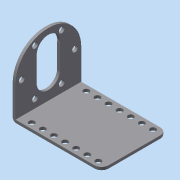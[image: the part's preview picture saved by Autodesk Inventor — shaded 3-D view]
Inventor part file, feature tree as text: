
AUTODESK INVENTOR PART (.ipt)
format: ipt  version: 2014 SP2 (Build 180246200, 246)  size: 179,712 bytes
history: native  units: mm
features: sketch x4, extrude x3, fillet x3, hole x1, pattern_linear x1
ambient origin geometry x8: Origin, YZ Plane, XZ Plane, XY Plane, X Axis, Y Axis, Z Axis, Center Point
bodies: Volumenkörper1 (feature_tree)
feature tree (12):
  extrude  "Extrusion1"  Depth=50.8mm
  extrude  "Extrusion2"  Depth=37.59mm
  extrude  "Extrusion3"  Depth=13.21mm
  fillet  "Rundung1"  Radius=11.0mm
  fillet  "Rundung2"  Radius=19.0mm
  fillet  "Rundung3"  Radius=30.5mm
  hole  "Bohrung2"  [1 undecoded]
  pattern_linear  "Rechteckige Anordnung1"  Spacing1=3.25mm  [1 undecoded]
  sketch  "Skizze1"  dims[d0=37.59mm d1=50.8mm]
  sketch  "Skizze2"  dims[d2=1.59mm d3=0.0mm d4=37.59mm]
  sketch  "Skizze4"  dims[d5=14.02mm d6=13.21mm d8=11.0mm d9=19.0mm d10=30.5mm]
  sketch  "Skizze5"  dims[d11=60.0mm d13=360.0deg d15=3.25mm d16=3.25mm d17=3.25mm d19=37.59mm d20=1.59mm d21=0.0mm d22=1.59mm d23=0.0mm d24=18.5mm d25=2.0mm d26=4.0mm d36=31.24mm d37=5.0mm d38=5.0mm d39=3.175mm d40=3.25mm d41=6.0mm d42=4.0mm d43=2.0mm d44=90.0deg d45=8.0mm d46=20.594885mm d47=70.0mm d49=6.35mm]
note: 2 required parameter values undecoded (feature->parameter linkage not recoverable at this tier; creation-order binding heuristic only, values carry confidence <= 0.55)
